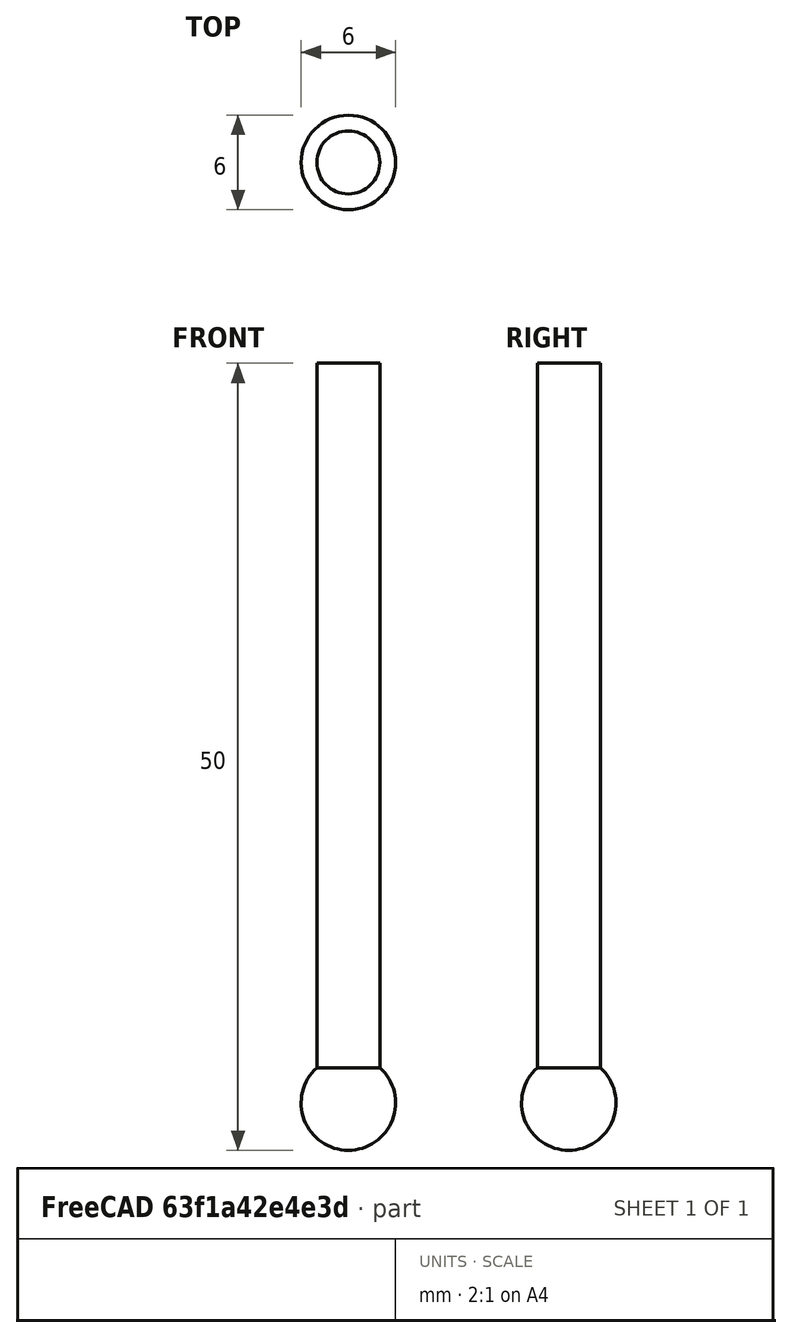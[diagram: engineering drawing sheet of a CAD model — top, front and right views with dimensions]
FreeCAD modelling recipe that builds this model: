
FCSTD DOCUMENT  (FreeCAD 0.21R32331 +3 (Git))
Label: probe
License: Creative Commons Attribution 4.0
LicenseURL: https://creativecommons.org/licenses/by/4.0/
objects: Sketcher::SketchObject×1, PartDesign::Revolution×1, App::FeaturePython×1, PartDesign::Body×1
note: 4 computed .brp shape members not serialized (recipe doc carries the construction recipe); baked Part::Feature solids carry a one-line shape summary decoded from their .brp

FEATURE [Sketcher::SketchObject] Sketch
  FullyConstrained = true
  MapMode = 5
  Placement = pos=(0,0,0) rot=(1,0,0;1.5708rad)
  Support = -> [XZ_Plane]
  expr: Constraints[11] = <<Attributes>>.Diameter
  expr: Constraints[15] = <<Attributes>>.Length
  expr: Constraints[8] = <<Attributes>>.ShaftDiameter
  sketch-geometry (6):
    g0: LineSegment StartX=-6e-16 StartY=0 StartZ=0 EndX=2 EndY=0 EndZ=0
    g1: LineSegment StartX=2 StartY=0 StartZ=0 EndX=2 EndY=-44.7639 EndZ=0
    g2: LineSegment StartX=-6e-16 StartY=-50 StartZ=0 EndX=-6e-16 EndY=0 EndZ=0
    g3: LineSegment StartX=-2 StartY=0 StartZ=0 EndX=2 EndY=0 EndZ=0
    g4: ArcOfCircle CenterX=0 CenterY=-47 CenterZ=0 NormalX=0 NormalY=0 NormalZ=1 AngleXU=0 Radius=3 StartAngle=4.71239 EndAngle=7.12425
    g5: LineSegment StartX=0 StartY=-47 StartZ=0 EndX=0 EndY=-53 EndZ=0
  constraints (16):
    c: Coincident(g0,g1)
    c: Coincident(g2,g0)
    c: Horizontal(g0)
    c: Vertical(g1)
    c: Vertical(g2)
    c: Coincident(g0,g-1)
    c: Symmetric(g3,g3,g-2)
    c: Coincident(g0,g3)
    c: DistanceX(g3,g3) = 4
    c: PointOnObject(g4,g2)
    c: Coincident(g4,g2)
    c: DistanceY(g5,g5) = 6
    c: Coincident(g5,g4)
    c: Coincident(g4,g1)
    c: Symmetric(g4,g5,g2)
    c: DistanceY(g2,g2) = 50
FEATURE [PartDesign::Revolution] Revolution
  AllowMultiFace = false
  Angle = 360
  Axis = (0,-2e-16,1)
  Base = (0,0,0)
  Placement = pos=(0,0,0) rot=(1,0,0;1.5708rad)
  Profile = -> Sketch
  ReferenceAxis = -> Sketch [V_Axis]
  Reversed = true
FEATURE [App::FeaturePython] PropertyBag  label="Attributes"  # WARN: FeaturePython — macro-defined, semantics opaque (R4)
  CustomPropertyGroups = Shape | Attributes
  Diameter = 6
  Length = 50
  ShaftDiameter = 4
  SpindlePower = false
FEATURE [PartDesign::Body] Body  label="Probe"
  Group = -> [Sketch,Revolution,PropertyBag]
  Origin = -> Origin
  Tip = -> Revolution
